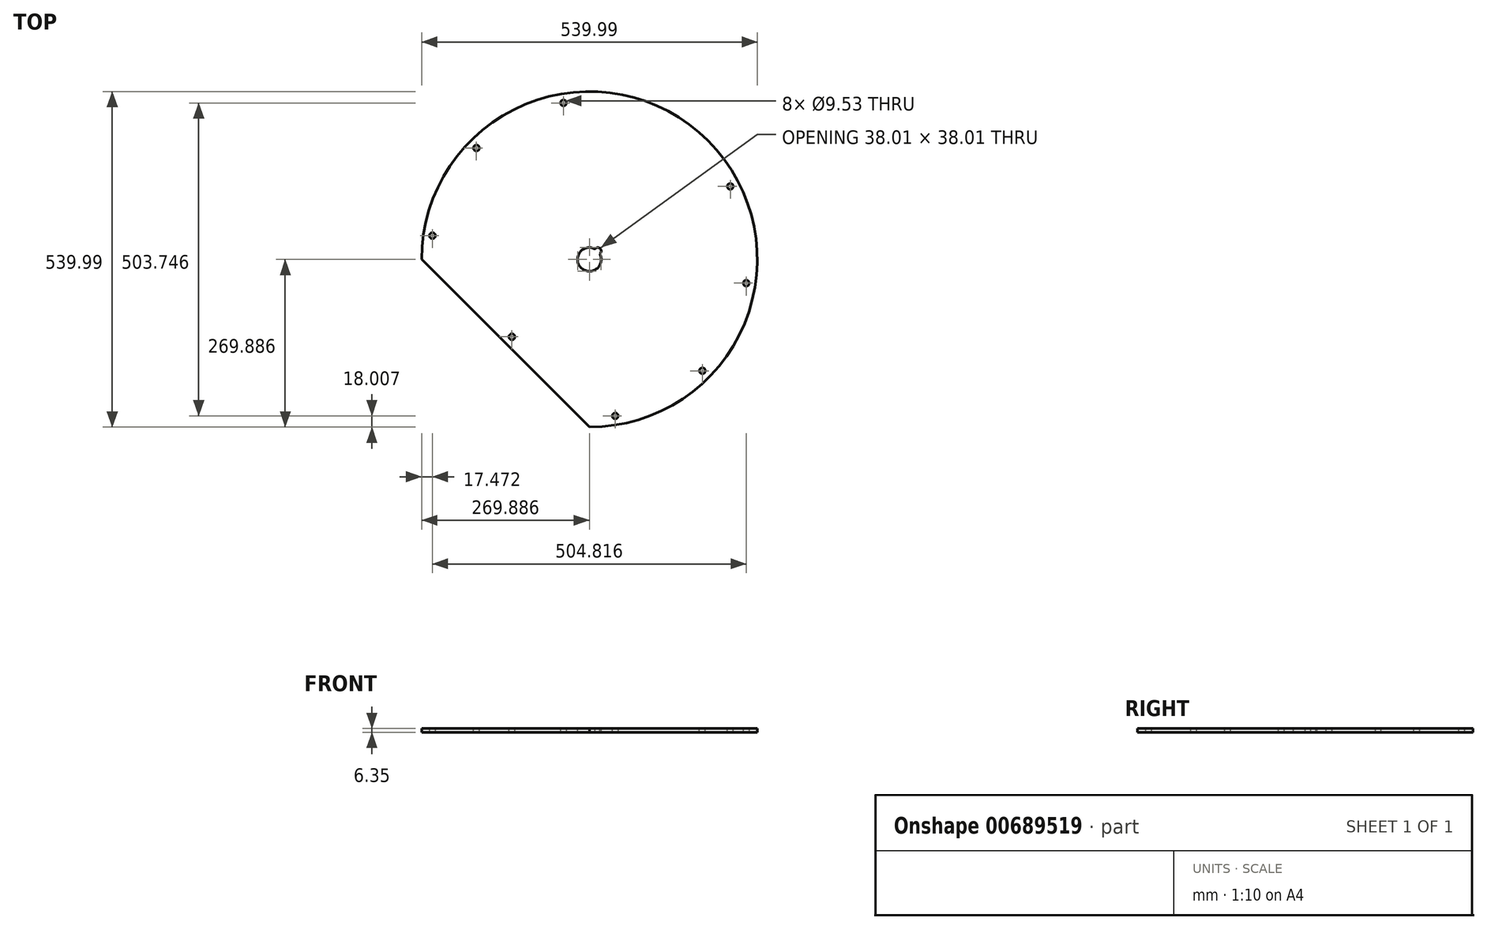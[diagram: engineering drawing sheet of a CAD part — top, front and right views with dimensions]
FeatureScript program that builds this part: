
annotation { "Feature Type Name" : "Feature", "Feature Type Description" : "" }
export const myFeature = defineFeature(function(context is Context, id is Id, definition is map)
    precondition{}
    {
        {
            var Q0;
            Q0=qCreatedBy(makeId("Top.planeOp"),FACE);
            var sketch = newSketch(context, id + "F0", { "sketchPlane" : qUnion([Q0])});
            skLineSegment(sketch, "E0", {"start": v(0, 0) * mm, "end": v(0, -269.88) * mm, "construction": true});
            skLineSegment(sketch, "E1", {"start": v(0, 0) * mm, "end": v(-269.88, 0) * mm, "construction": true});
            skLineSegment(sketch, "E2", {"start": v(0, 0) * mm, "end": v(269.88, 0) * mm, "construction": true});
            skArc(sketch, "E3", {"start": v(0, -269.88) * mm, "mid": v(191.03, 191.03) * mm, "end": v(-269.88, 0) * mm});
            skLineSegment(sketch, "E4", {"start": v(0, 0) * mm, "end": v(0, 270.11) * mm, "construction": true});
            skLineSegment(sketch, "E5", {"start": v(-269.88, 0) * mm, "end": v(0, -269.88) * mm});
            skCircle(sketch, "E6", {"center": v(0, 0) * mm, "radius": 19.05 * mm});
            skLineSegment(sketch, "E7", {"start": v(0, 0) * mm, "end": v(-134.94, -134.94) * mm, "construction": true});
            skArc(sketch, "E8.0", {"start": v(0, -255.27) * mm, "mid": v(180.7, 180.7) * mm, "end": v(-255.27, 0) * mm, "construction": true});
            skCircle(sketch, "E9", {"center": v(-252.4, 38.25) * mm, "radius": 4.76 * mm});
            skCircle(sketch, "E10.1.0", {"center": v(-181.72, 179.3) * mm, "radius": 4.76 * mm});
            skCircle(sketch, "E10.2.0", {"center": v(-41.62, 251.87) * mm, "radius": 4.76 * mm});
            skCircle(sketch, "E10.4.0", {"center": v(226.68, 117.42) * mm, "radius": 4.76 * mm});
            skCircle(sketch, "E10.5.0", {"center": v(252.4, -38.25) * mm, "radius": 4.76 * mm});
            skCircle(sketch, "E10.6.0", {"center": v(181.72, -179.3) * mm, "radius": 4.76 * mm});
            skCircle(sketch, "E10.7.0", {"center": v(41.62, -251.87) * mm, "radius": 4.76 * mm});
            skLineSegment(sketch, "E10.anchor1", {"start": v(0, 0) * mm, "end": v(-252.4, 38.25) * mm, "construction": true});
            skLineSegment(sketch, "E10.anchor2", {"start": v(0, 0) * mm, "end": v(41.62, -251.87) * mm, "construction": true});
            skLineSegment(sketch, "E11.0", {"start": v(-249.22, 0) * mm, "end": v(0, -249.22) * mm, "construction": true});
            skCircle(sketch, "E12", {"center": v(-124.61, -124.61) * mm, "radius": 4.76 * mm});
            skCircle(sketch, "E13", {"center": v(13.47, 13.47) * mm, "radius": 5.56 * mm});
            skLineSegment(sketch, "E14", {"start": v(0, 0) * mm, "end": v(13.47, 13.47) * mm, "construction": true});
            skSolve(sketch);
        }
        {
            var Q0;
            Q0=makeQuery(id+"F0.imprint","IMPRINT",FACE,{"disambiguationData":[TD([[makeQuery(id+"F0.imprint","IMPRINT",EDGE,{"derivedFrom":sQuery(id+"F0.wireOp",EDGE,"E3")}),1.0]])]});
            extrude(context, id + "F1", {"entities" : qUnion([Q0]), "oppositeDirection" : true, "depth" : 6.35 * mm, "offsetDistance" : 25.4 * mm});
        }
    });
